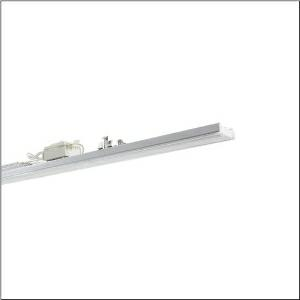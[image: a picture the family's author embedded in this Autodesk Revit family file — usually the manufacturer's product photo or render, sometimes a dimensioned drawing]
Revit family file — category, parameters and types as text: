
# Revit family: licross_r__11_recessed_ho_51tl11dv4m2s_9ec1
name_source: partatom
category: Lighting Fixtures
units: mm (PartAtom-declared; Revit-internal decimal feet)

## family parameters
Cut with Voids When Loaded = No
Host = Face
Light Source = No
Part Type = Normal
Room Calculation Point = No
Round Connector Dimension = Use Diameter
Shared = No

## types (1)
- --- (1 x LED, 27080 lm, 150.5 W, 4000K)
    Apparent Load = 150 VA
    CIE Flux Codes = 87 95 99 100 100
    Color Rendering = 80
    Color Temperature = 4000K
    Default Elevation = 1800 mm
    Description = Licross® 11 Recessed HO, luminaire insert, of sheet steel, coil coated, white, length: 2.250mm, width: 66mm, height: 67mm, LED rated luminous flux: 27.080lm, light colour: 840, control gear: DALI 2, with plug, 5-pole, with phase selection, mains connection: 220..240V, AC, 50/60Hz, rated input power: 151W, halogen-free wiring, primary light control with lens, of plastic, primary optical cover: cover, of PMMA, light emission: direct distribution, primary light characteristic: symmetric, protection rating (complete): IP40, insulation class (complete): insulation class I (protective earthing), certification: CE, ENEC, VDE, UKCA, protection symbol: D if used in an environment without relevant dust loads with corresponding accessories, impact resistance: IK06, permissible ambient temperature for indoor applications: -40..+35°C, corresponds to IFS (International Featured Standards) requirements for safety and quality in the food industry, reducing of maximum allowable ambient temperature of 5°C with ceiling mounting, LABS conformity tested according to VDMA 24364:2018-05, packaging unit: 1 piece
    Height = 58 mm
    Lamp = 1 x LED
    Lamp Light Flux = 27080 lm
    Lamp Power = 150.5 W
    Lamp count = 1
    Length = 2250 mm
    Luminous efficacy = 180 lm/W
    Manufacturer = Siteco
    ModVariant = No
    Model = 51TL11DV4M2S
    Mounting Place = Ceiling
    Mounting Type = Pendant
    Number of Poles = 1
    OnlyDefault = Yes
    Power Factor = 1
    Product Name = Licross® 11 Recessed HO
    Product group = luminaire insert
    ProductGroupID = 902
    Protection Class = Protection class I
    Protection Degree = IP 40
    RLX_Detail_Level = 1
    RLX_Emergency_Light_Flux = 0 lm
    RLX_Emergency_Type = 0
    RLX_Emergency_Type_DB = No
    RlxData = <blob elided: 29469 chars, md5=47072786>
    Socket = socket
    Standby Power = 0 W
    System Light Flux = 27079 lm
    System Power = 150 W
    Type Comments = factory setting: luminous flux: 100 % | dim-lin: 254 | 690 mA
    Type Image = l_1296930.jpg
    URL = http://relux.com
    VarID = @adj_098864
    Voltage = 0 V
    Weight = 0.00 kg
    Width = 66 mm

## geometry (parser evidence)
native form markers: Blend x4, Sweep x12
no freeform markers — native parametric forms only
